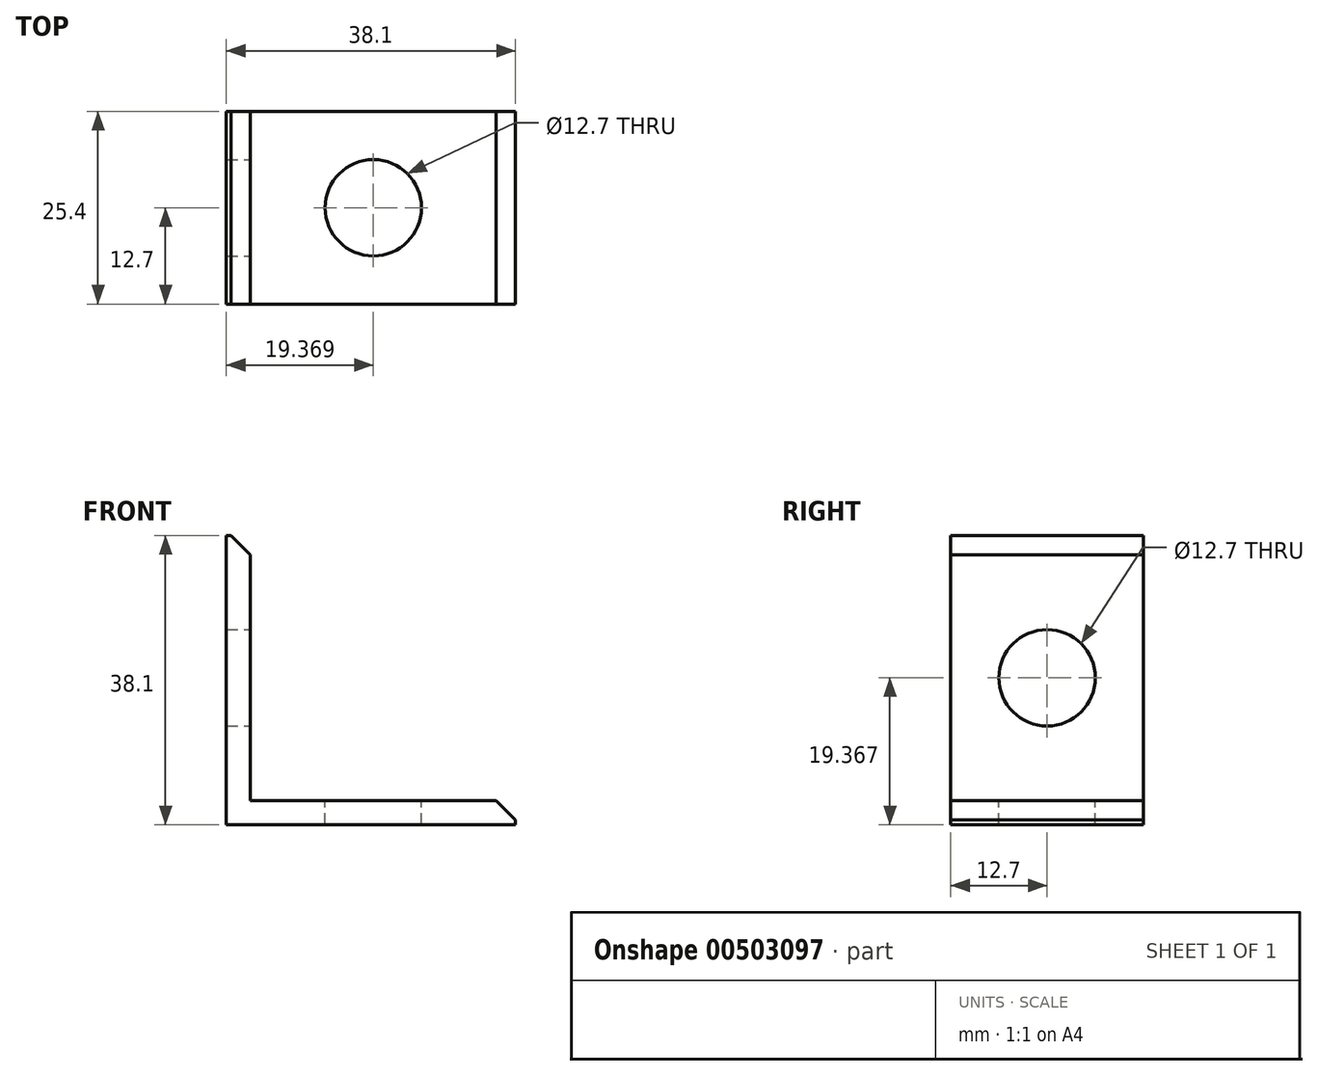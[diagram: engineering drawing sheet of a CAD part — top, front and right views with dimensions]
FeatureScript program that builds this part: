
annotation { "Feature Type Name" : "Feature", "Feature Type Description" : "" }
export const myFeature = defineFeature(function(context is Context, id is Id, definition is map)
    precondition{}
    {
        {
            var Q0;
            Q0=qCreatedBy(makeId("Front.planeOp"),FACE);
            var sketch = newSketch(context, id + "F0", { "sketchPlane" : qUnion([Q0])});
            skLineSegment(sketch, "E0.bottom", {"start": v(-67.5, 25.45) * mm, "end": v(-64.33, 25.45) * mm});
            skLineSegment(sketch, "E0.top", {"start": v(-67.5, -12.65) * mm, "end": v(-29.4, -12.65) * mm});
            skLineSegment(sketch, "E0.left", {"start": v(-67.5, 25.45) * mm, "end": v(-67.5, -12.65) * mm});
            skLineSegment(sketch, "E0.right", {"start": v(-29.4, -9.48) * mm, "end": v(-29.4, -12.65) * mm});
            skPoint(sketch, "E1", {"position": v(-64.33, 25.45) * mm});
            skPoint(sketch, "E2", {"position": v(-29.4, -9.48) * mm});
            skLineSegment(sketch, "E3", {"start": v(-64.33, 25.45) * mm, "end": v(-64.33, -9.48) * mm});
            skLineSegment(sketch, "E4", {"start": v(-64.33, -9.48) * mm, "end": v(-29.4, -9.48) * mm});
            skSolve(sketch);
        }
        {
            var Q0;
            Q0=makeQuery(id+"F0.imprint","IMPRINT",FACE,{"disambiguationData":[TD([[makeQuery(id+"F0.imprint","IMPRINT",EDGE,{"derivedFrom":sQuery(id+"F0.wireOp",EDGE,"E0.bottom")}),-1.0]])]});
            extrude(context, id + "F1", {"entities" : qUnion([Q0]), "depth" : 25.4 * mm});
        }
        {
            var Q0;
            Q0=makeQuery(id+"F1.opExtrude","SWEPT_EDGE",EDGE,{"disambiguationData":[OSD([sQuery(id+"F0.wireOp",EDGE,"E0.bottom"),sQuery(id+"F0.wireOp",EDGE,"E3")])]});
            chamfer(context, id + "F2", {"entities" : qUnion([Q0]), "width" : 2.54 * mm, "tangentPropagation" : true});
        }
        {
            var Q0;
            Q0=makeQuery(id+"F1.opExtrude","SWEPT_EDGE",EDGE,{"disambiguationData":[OSD([sQuery(id+"F0.wireOp",EDGE,"E0.right"),sQuery(id+"F0.wireOp",EDGE,"E4")])]});
            chamfer(context, id + "F3", {"entities" : qUnion([Q0]), "width" : 2.54 * mm, "tangentPropagation" : true});
        }
        {
            var Q0;
            Q0=makeQuery(id+"F1.opExtrude","SWEPT_FACE",FACE,{"disambiguationData":[OSD([sQuery(id+"F0.wireOp",EDGE,"E3")])]});
            var sketch = newSketch(context, id + "F4", { "sketchPlane" : qUnion([Q0])});
            skLineSegment(sketch, "E5", {"start": v(-12.7, 22.9) * mm, "end": v(-12.7, -9.48) * mm, "construction": true});
            skLineSegment(sketch, "E6", {"start": v(-25.4, 6.72) * mm, "end": v(0, 6.72) * mm, "construction": true});
            skCircle(sketch, "E7", {"center": v(-12.7, 6.72) * mm, "radius": 6.35 * mm});
            skSolve(sketch);
        }
        {
            var Q0;
            Q0=makeQuery(id+"F1.opExtrude","SWEPT_FACE",FACE,{"disambiguationData":[OSD([sQuery(id+"F0.wireOp",EDGE,"E4")])]});
            var sketch = newSketch(context, id + "F5", { "sketchPlane" : qUnion([Q0])});
            skLineSegment(sketch, "E8", {"start": v(-64.33, -12.7) * mm, "end": v(-31.95, -12.7) * mm, "construction": true});
            skLineSegment(sketch, "E9", {"start": v(-48.14, -25.4) * mm, "end": v(-48.14, -1.1) * mm, "construction": true});
            skPoint(sketch, "E9.endSnap0", {"position": v(-48.14, 0) * mm});
            skCircle(sketch, "E10", {"center": v(-48.14, -12.7) * mm, "radius": 6.35 * mm});
            skSolve(sketch);
        }
        {
            var Q0;
            Q0=makeQuery(id+"F4.imprint","IMPRINT",FACE,{"disambiguationData":[TD([[makeQuery(id+"F4.imprint","IMPRINT",EDGE,{"derivedFrom":sQuery(id+"F4.wireOp",EDGE,"E7")}),1.0]])]});
            extrude(context, id + "F6", {"entities" : qUnion([Q0]), "operationType" : NewBodyOperationType.REMOVE, "endBound" : BoundingType.THROUGH_ALL, "oppositeDirection" : true, "depth" : 25.4 * mm});
        }
        {
            var Q0;
            Q0=makeQuery(id+"F5.imprint","IMPRINT",FACE,{"disambiguationData":[TD([[makeQuery(id+"F5.imprint","IMPRINT",EDGE,{"derivedFrom":sQuery(id+"F5.wireOp",EDGE,"E10")}),1.0]])]});
            extrude(context, id + "F7", {"entities" : qUnion([Q0]), "operationType" : NewBodyOperationType.REMOVE, "endBound" : BoundingType.THROUGH_ALL, "oppositeDirection" : true, "depth" : 25.4 * mm});
        }
    });
